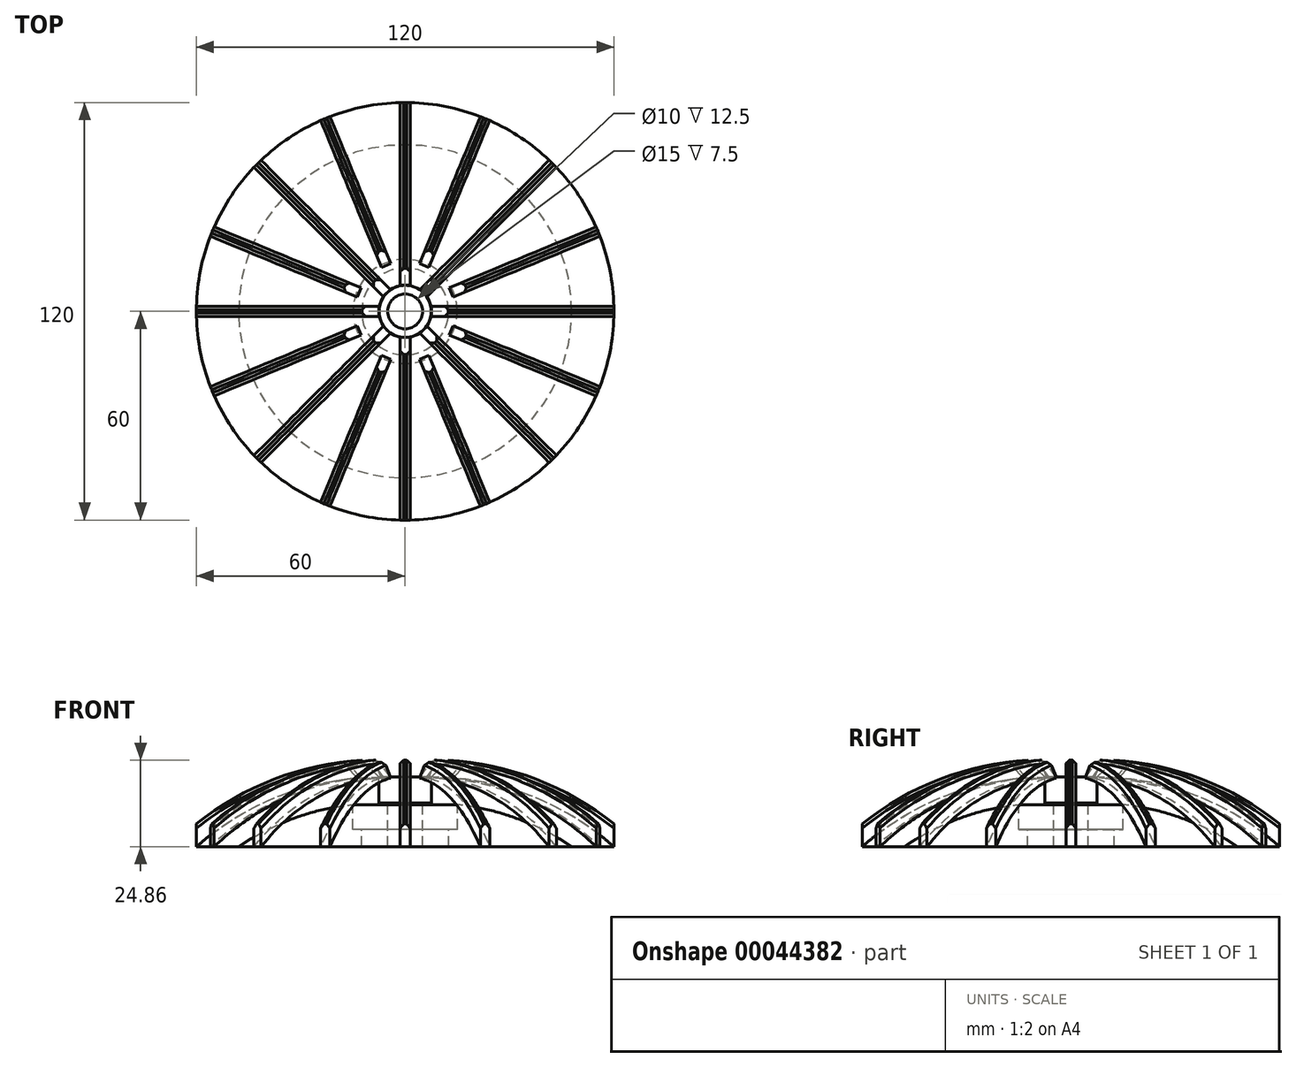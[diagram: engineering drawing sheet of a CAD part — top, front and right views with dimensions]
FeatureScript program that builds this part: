
annotation { "Feature Type Name" : "Feature", "Feature Type Description" : "" }
export const myFeature = defineFeature(function(context is Context, id is Id, definition is map)
    precondition{}
    {
        {
            var Q0;
            Q0=qCreatedBy(makeId("Right.planeOp"),FACE);
            var sketch = newSketch(context, id + "F0", { "sketchPlane" : qUnion([Q0])});
            skLineSegment(sketch, "E0", {"start": v(0, 38.83) * mm, "end": v(0, -39.1) * mm, "construction": true});
            skLineSegment(sketch, "E1", {"start": v(-69.96, 0) * mm, "end": v(68.9, 0) * mm, "construction": true});
            skLineSegment(sketch, "E2", {"start": v(-60, 0) * mm, "end": v(-47.86, 0) * mm});
            skLineSegment(sketch, "E3", {"start": v(-5, 0) * mm, "end": v(-5, 12.5) * mm});
            skLineSegment(sketch, "E4", {"start": v(-5, 12.5) * mm, "end": v(-7.5, 12.5) * mm});
            skLineSegment(sketch, "E5", {"start": v(-7.5, 12.5) * mm, "end": v(-7.5, 20) * mm});
            skLineSegment(sketch, "E6", {"start": v(-7.5, 20) * mm, "end": v(0, 20) * mm, "construction": true});
            skArc(sketch, "E7", {"start": v(-7.5, 20) * mm, "mid": v(-35.6, 14.83) * mm, "end": v(-60, 0) * mm});
            skArc(sketch, "E8.0", {"start": v(-15, 12.1) * mm, "mid": v(-32.18, 8.1) * mm, "end": v(-47.86, 0) * mm});
            skLineSegment(sketch, "E9.0", {"start": v(-2.5, 17.5) * mm, "end": v(-2.5, 20) * mm});
            skLineSegment(sketch, "E9.1", {"start": v(0, 17.5) * mm, "end": v(-2.5, 17.5) * mm});
            skLineSegment(sketch, "E9.2", {"start": v(0, 0) * mm, "end": v(0, 17.5) * mm});
            skLineSegment(sketch, "E10", {"start": v(-15, 12.1) * mm, "end": v(-15, 5) * mm});
            skLineSegment(sketch, "E11", {"start": v(-15, 5) * mm, "end": v(-12.5, 5) * mm});
            skLineSegment(sketch, "E12", {"start": v(-12.5, 5) * mm, "end": v(-12.5, 0) * mm});
            skLineSegment(sketch, "E13.trimOffspring", {"start": v(-12.5, 0) * mm, "end": v(-5, 0) * mm});
            skSolve(sketch);
        }
        {
            var Q0;
            Q0=makeQuery(id+"F0.imprint","IMPRINT",FACE,{"disambiguationData":[TD([[makeQuery(id+"F0.imprint","IMPRINT",EDGE,{"derivedFrom":sQuery(id+"F0.wireOp",EDGE,"E2")}),1.0]])]});
            var Q1;
            Q1=sQuery(id+"F0.wireOp",EDGE,"E0");
            revolve(context, id + "F1", {"entities" : qUnion([Q0]), "axis" : qUnion([Q1]), "revolveType" : RevolveType.FULL});
        }
        {
            var Q0;
            Q0=qCreatedBy(makeId("Right.planeOp"),FACE);
            var sketch = newSketch(context, id + "F2", { "sketchPlane" : qUnion([Q0])});
            skLineSegment(sketch, "E14.0", {"start": v(-7.5, 20) * mm, "end": v(7.5, 20) * mm, "construction": true});
            skLineSegment(sketch, "E15.0", {"start": v(-7.5, 12.5) * mm, "end": v(7.5, 12.5) * mm, "construction": true});
            skLineSegment(sketch, "E16.0", {"start": v(-60, 0) * mm, "end": v(60, 0) * mm, "construction": true});
            skArc(sketch, "E17", {"start": v(-7.5, 20) * mm, "mid": v(-35.6, 14.83) * mm, "end": v(-60, 0) * mm, "construction": true});
            skArc(sketch, "E18.0", {"start": v(-12.36, 24.86) * mm, "mid": v(-37.6, 19.41) * mm, "end": v(-60, 6.55) * mm});
            skArc(sketch, "E19.0", {"start": v(-7.5, 17) * mm, "mid": v(-32.9, 12.62) * mm, "end": v(-55.37, 0) * mm});
            skLineSegment(sketch, "E20", {"start": v(-60, 0) * mm, "end": v(-55.37, 0) * mm});
            skLineSegment(sketch, "E21", {"start": v(-60, 0) * mm, "end": v(-60, 6.55) * mm});
            skLineSegment(sketch, "E22", {"start": v(-7.5, 20) * mm, "end": v(-7.5, 17) * mm});
            skLineSegment(sketch, "E23", {"start": v(-7.5, 20) * mm, "end": v(-12.36, 24.86) * mm});
            skSolve(sketch);
        }
        {
            var Q0;
            Q0 = qSketchRegion(id + "F2", true);
            extrude(context, id + "F3", {"entities" : qUnion([Q0]), "endBound" : BoundingType.SYMMETRIC, "depth" : 2.9 * mm});
        }
        {
            var Q0;
            Q0=makeQuery(id+"F3.opExtrude","CAP_EDGE",EDGE,{"disambiguationData":[OSD([sQuery(id+"F2.wireOp",EDGE,"E18.0")])],"isStart":true});
            var Q1;
            Q1=makeQuery(id+"F3.opExtrude","CAP_EDGE",EDGE,{"disambiguationData":[OSD([sQuery(id+"F2.wireOp",EDGE,"E18.0")])],"isStart":false});
            chamfer(context, id + "F4", {"entities" : qUnion([Q0, Q1]), "width" : 1 * mm, "tangentPropagation" : true});
        }
        {
            var Q0;
            Q0=makeQuery(id+"F3.opExtrude","SWEPT_BODY",BODY,{"disambiguationData":[OSD([sQuery(id+"F2.wireOp",EDGE,"E18.0"),sQuery(id+"F2.wireOp",EDGE,"E19.0"),sQuery(id+"F2.wireOp",EDGE,"E20"),sQuery(id+"F2.wireOp",EDGE,"E21"),sQuery(id+"F2.wireOp",EDGE,"E22"),sQuery(id+"F2.wireOp",EDGE,"E23")])]});
            var Q1;
            Q1=makeQuery(id+"F1.opRevolve","SWEPT_FACE",FACE,{"disambiguationData":[OSD([sQuery(id+"F0.wireOp",EDGE,"E5")])]});
            circularPattern(context, id + "F5", {"entities" : qUnion([Q0]), "axis" : qUnion([Q1]), "angle" : 360 * degree, "instanceCount" : 8, "equalSpace" : true});
        }
        {
            var Q0;
            Q0=makeQuery(id+"F1.opRevolve","SWEPT_BODY",BODY,{"disambiguationData":[OSD([sQuery(id+"F0.wireOp",EDGE,"E2"),sQuery(id+"F0.wireOp",EDGE,"E3"),sQuery(id+"F0.wireOp",EDGE,"E4"),sQuery(id+"F0.wireOp",EDGE,"E5"),sQuery(id+"F0.wireOp",EDGE,"E7"),sQuery(id+"F0.wireOp",EDGE,"E8.0"),sQuery(id+"F0.wireOp",EDGE,"E10"),sQuery(id+"F0.wireOp",EDGE,"E11"),sQuery(id+"F0.wireOp",EDGE,"E12"),sQuery(id+"F0.wireOp",EDGE,"E13.trimOffspring")])]});
            var Q1;
            Q1=makeQuery(id+"F3.opExtrude","SWEPT_BODY",BODY,{"disambiguationData":[OSD([sQuery(id+"F2.wireOp",EDGE,"E18.0"),sQuery(id+"F2.wireOp",EDGE,"E19.0"),sQuery(id+"F2.wireOp",EDGE,"E20"),sQuery(id+"F2.wireOp",EDGE,"E21"),sQuery(id+"F2.wireOp",EDGE,"E22"),sQuery(id+"F2.wireOp",EDGE,"E23")])]});
            var Q2;
            Q2=makeQuery(id+"F5.opPattern","COPY",BODY,{"derivedFrom":makeQuery(id+"F3.opExtrude","SWEPT_BODY",BODY,{"disambiguationData":[OSD([sQuery(id+"F2.wireOp",EDGE,"E18.0"),sQuery(id+"F2.wireOp",EDGE,"E19.0"),sQuery(id+"F2.wireOp",EDGE,"E20"),sQuery(id+"F2.wireOp",EDGE,"E21"),sQuery(id+"F2.wireOp",EDGE,"E22"),sQuery(id+"F2.wireOp",EDGE,"E23")])]}),"instanceName":"1"});
            var Q3;
            Q3=makeQuery(id+"F5.opPattern","COPY",BODY,{"derivedFrom":makeQuery(id+"F3.opExtrude","SWEPT_BODY",BODY,{"disambiguationData":[OSD([sQuery(id+"F2.wireOp",EDGE,"E18.0"),sQuery(id+"F2.wireOp",EDGE,"E19.0"),sQuery(id+"F2.wireOp",EDGE,"E20"),sQuery(id+"F2.wireOp",EDGE,"E21"),sQuery(id+"F2.wireOp",EDGE,"E22"),sQuery(id+"F2.wireOp",EDGE,"E23")])]}),"instanceName":"2"});
            var Q4;
            Q4=makeQuery(id+"F5.opPattern","COPY",BODY,{"derivedFrom":makeQuery(id+"F3.opExtrude","SWEPT_BODY",BODY,{"disambiguationData":[OSD([sQuery(id+"F2.wireOp",EDGE,"E18.0"),sQuery(id+"F2.wireOp",EDGE,"E19.0"),sQuery(id+"F2.wireOp",EDGE,"E20"),sQuery(id+"F2.wireOp",EDGE,"E21"),sQuery(id+"F2.wireOp",EDGE,"E22"),sQuery(id+"F2.wireOp",EDGE,"E23")])]}),"instanceName":"3"});
            var Q5;
            Q5=makeQuery(id+"F5.opPattern","COPY",BODY,{"derivedFrom":makeQuery(id+"F3.opExtrude","SWEPT_BODY",BODY,{"disambiguationData":[OSD([sQuery(id+"F2.wireOp",EDGE,"E18.0"),sQuery(id+"F2.wireOp",EDGE,"E19.0"),sQuery(id+"F2.wireOp",EDGE,"E20"),sQuery(id+"F2.wireOp",EDGE,"E21"),sQuery(id+"F2.wireOp",EDGE,"E22"),sQuery(id+"F2.wireOp",EDGE,"E23")])]}),"instanceName":"4"});
            var Q6;
            Q6=makeQuery(id+"F5.opPattern","COPY",BODY,{"derivedFrom":makeQuery(id+"F3.opExtrude","SWEPT_BODY",BODY,{"disambiguationData":[OSD([sQuery(id+"F2.wireOp",EDGE,"E18.0"),sQuery(id+"F2.wireOp",EDGE,"E19.0"),sQuery(id+"F2.wireOp",EDGE,"E20"),sQuery(id+"F2.wireOp",EDGE,"E21"),sQuery(id+"F2.wireOp",EDGE,"E22"),sQuery(id+"F2.wireOp",EDGE,"E23")])]}),"instanceName":"5"});
            var Q7;
            Q7=makeQuery(id+"F5.opPattern","COPY",BODY,{"derivedFrom":makeQuery(id+"F3.opExtrude","SWEPT_BODY",BODY,{"disambiguationData":[OSD([sQuery(id+"F2.wireOp",EDGE,"E18.0"),sQuery(id+"F2.wireOp",EDGE,"E19.0"),sQuery(id+"F2.wireOp",EDGE,"E20"),sQuery(id+"F2.wireOp",EDGE,"E21"),sQuery(id+"F2.wireOp",EDGE,"E22"),sQuery(id+"F2.wireOp",EDGE,"E23")])]}),"instanceName":"6"});
            var Q8;
            Q8=makeQuery(id+"F5.opPattern","COPY",BODY,{"derivedFrom":makeQuery(id+"F3.opExtrude","SWEPT_BODY",BODY,{"disambiguationData":[OSD([sQuery(id+"F2.wireOp",EDGE,"E18.0"),sQuery(id+"F2.wireOp",EDGE,"E19.0"),sQuery(id+"F2.wireOp",EDGE,"E20"),sQuery(id+"F2.wireOp",EDGE,"E21"),sQuery(id+"F2.wireOp",EDGE,"E22"),sQuery(id+"F2.wireOp",EDGE,"E23")])]}),"instanceName":"7"});
            booleanBodies(context, id + "F6", {"operationType" : BooleanOperationType.UNION, "tools" : qUnion([Q0, Q1, Q2, Q3, Q4, Q5, Q6, Q7, Q8])});
        }
        {
            var Q0;
            Q0=makeQuery(id+"F1.opRevolve","SWEPT_FACE",FACE,{"disambiguationData":[OSD([sQuery(id+"F0.wireOp",EDGE,"E4")])]});
            var sketch = newSketch(context, id + "F7", { "sketchPlane" : qUnion([Q0])});
            skFitSpline(sketch, "E24.0.0", {"points": [v(-6.33, 4.28) * mm, v(-18.7, 16.65) * mm, v(-31.07, 29.02) * mm, v(-43.44, 41.39) * mm]});
            skArc(sketch, "E24.0.1", {"start": v(-43.44, 41.39) * mm, "mid": v(-55.43, 22.96) * mm, "end": v(-59.98, 1.45) * mm});
            skFitSpline(sketch, "E24.0.2", {"points": [v(-59.98, 1.45) * mm, v(-42.49, 1.45) * mm, v(-25, 1.45) * mm, v(-7.5, 1.45) * mm]});
            skFitSpline(sketch, "E24.0.3", {"points": [v(-7.5, 1.45) * mm, v(-7.5, 0.97) * mm, v(-7.5, 0.48) * mm, v(-7.5, 0) * mm]});
            skArc(sketch, "E24.0.4", {"start": v(-7.5, 0) * mm, "mid": v(-6.93, 2.87) * mm, "end": v(-5.3, 5.3) * mm});
            skFitSpline(sketch, "E24.0.5", {"points": [v(-5.3, 5.3) * mm, v(-5.65, 4.96) * mm, v(-5.99, 4.62) * mm, v(-6.33, 4.28) * mm]});
            skPoint(sketch, "E25.startSnap0", {"position": v(-6.93, 2.87) * mm});
            skLineSegment(sketch, "E26", {"start": v(-6.93, 2.87) * mm, "end": v(-55.43, 22.96) * mm});
            skLineSegment(sketch, "E27.0", {"start": v(-6.37, 4.2) * mm, "end": v(-54.88, 24.3) * mm});
            skLineSegment(sketch, "E28.0", {"start": v(-7.48, 1.53) * mm, "end": v(-55.99, 21.62) * mm});
            skLineSegment(sketch, "E29.0", {"start": v(-5.26, 6.89) * mm, "end": v(-53.77, 26.98) * mm});
            skLineSegment(sketch, "E30.0", {"start": v(-8.6, -1.15) * mm, "end": v(-57.1, 18.94) * mm});
            skLineSegment(sketch, "E31", {"start": v(-11.54, 9.49) * mm, "end": v(-14.87, 1.45) * mm});
            skSolve(sketch);
        }
        {
            var Q0;
            Q0=sQuery(id+"F7.wireOp",EDGE,"E26");
            cPlane(context, id + "F8", {"entities" : qUnion([Q0]), "cplaneType" : CPlaneType.LINE_ANGLE, "offset" : 150 * mm, "angle" : 0 * degree, "width" : 150 * mm, "height" : 150 * mm});
        }
        {
            var Q0;
            Q0=qCreatedBy(id+"F8.planeOp",FACE);
            var sketch = newSketch(context, id + "F9", { "sketchPlane" : qUnion([Q0])});
            skLineSegment(sketch, "E32", {"start": v(7.5, 20) * mm, "end": v(7.5, 12.5) * mm});
            skLineSegment(sketch, "E33", {"start": v(-7.5, 12.5) * mm, "end": v(-7.5, 20) * mm});
            skLineSegment(sketch, "E34.0.0", {"start": v(55.97, 0) * mm, "end": v(55.99, 0) * mm});
            skLineSegment(sketch, "E34.0.1", {"start": v(55.99, 0) * mm, "end": v(54.88, 0) * mm});
            skLineSegment(sketch, "E34.0.2", {"start": v(54.88, 0) * mm, "end": v(54.86, 0) * mm});
            skLineSegment(sketch, "E34.0.3", {"start": v(54.86, 0) * mm, "end": v(24.3, 0) * mm});
            skLineSegment(sketch, "E34.0.4", {"start": v(24.3, 0) * mm, "end": v(24.3, 0) * mm});
            skLineSegment(sketch, "E34.0.5", {"start": v(24.3, 0) * mm, "end": v(21.62, 0) * mm});
            skLineSegment(sketch, "E34.0.6", {"start": v(21.62, 0) * mm, "end": v(21.61, 0) * mm});
            skLineSegment(sketch, "E34.0.7", {"start": v(21.61, 0) * mm, "end": v(-21.61, 0) * mm});
            skLineSegment(sketch, "E34.0.8", {"start": v(-21.61, 0) * mm, "end": v(-21.62, 0) * mm});
            skLineSegment(sketch, "E34.0.9", {"start": v(-21.62, 0) * mm, "end": v(-24.3, 0) * mm});
            skLineSegment(sketch, "E34.0.10", {"start": v(-24.3, 0) * mm, "end": v(-24.3, 0) * mm});
            skLineSegment(sketch, "E34.0.11", {"start": v(-24.3, 0) * mm, "end": v(-54.86, 0) * mm});
            skLineSegment(sketch, "E34.0.12", {"start": v(-54.86, 0) * mm, "end": v(-54.88, 0) * mm});
            skLineSegment(sketch, "E34.0.13", {"start": v(-54.88, 0) * mm, "end": v(-55.99, 0) * mm});
            skLineSegment(sketch, "E34.0.14", {"start": v(-55.99, 0) * mm, "end": v(-55.97, 0) * mm});
            skLineSegment(sketch, "E34.0.15", {"start": v(-55.97, 0) * mm, "end": v(-60, 0) * mm});
            skLineSegment(sketch, "E34.0.16", {"start": v(-55.97, 0) * mm, "end": v(-55.99, 0) * mm});
            skLineSegment(sketch, "E34.0.17", {"start": v(-55.99, 0) * mm, "end": v(-54.88, 0) * mm});
            skLineSegment(sketch, "E34.0.18", {"start": v(-54.88, 0) * mm, "end": v(-54.86, 0) * mm});
            skLineSegment(sketch, "E34.0.19", {"start": v(-24.3, 0) * mm, "end": v(-54.86, 0) * mm});
            skLineSegment(sketch, "E34.0.20", {"start": v(-24.3, 0) * mm, "end": v(-24.3, 0) * mm});
            skLineSegment(sketch, "E34.0.21", {"start": v(-24.3, 0) * mm, "end": v(-21.62, 0) * mm});
            skLineSegment(sketch, "E34.0.22", {"start": v(-21.62, 0) * mm, "end": v(-21.61, 0) * mm});
            skLineSegment(sketch, "E34.0.23", {"start": v(21.61, 0) * mm, "end": v(-21.61, 0) * mm});
            skLineSegment(sketch, "E34.0.24", {"start": v(21.61, 0) * mm, "end": v(21.62, 0) * mm});
            skLineSegment(sketch, "E34.0.25", {"start": v(21.62, 0) * mm, "end": v(24.3, 0) * mm});
            skLineSegment(sketch, "E34.0.26", {"start": v(24.3, 0) * mm, "end": v(24.3, 0) * mm});
            skLineSegment(sketch, "E34.0.27", {"start": v(54.86, 0) * mm, "end": v(24.3, 0) * mm});
            skLineSegment(sketch, "E34.0.28", {"start": v(54.86, 0) * mm, "end": v(54.88, 0) * mm});
            skLineSegment(sketch, "E34.0.29", {"start": v(54.88, 0) * mm, "end": v(55.99, 0) * mm});
            skLineSegment(sketch, "E34.0.30", {"start": v(55.99, 0) * mm, "end": v(55.97, 0) * mm});
            skLineSegment(sketch, "E34.0.31", {"start": v(60, 0) * mm, "end": v(55.97, 0) * mm});
            skLineSegment(sketch, "E35", {"start": v(-7.5, 20) * mm, "end": v(7.5, 20) * mm});
            skPoint(sketch, "E36.0", {"position": v(-14.3, 12.5) * mm});
            skLineSegment(sketch, "E37", {"start": v(-14.3, 12.5) * mm, "end": v(-14.3, 32.48) * mm, "construction": true});
            skArc(sketch, "E38", {"start": v(-7.5, 20) * mm, "mid": v(-35.6, 14.83) * mm, "end": v(-60, 0) * mm, "construction": true});
            skArc(sketch, "E39", {"start": v(-14.3, 19.7) * mm, "mid": v(-38.74, 13.55) * mm, "end": v(-60, 0) * mm});
            skArc(sketch, "E40.0", {"start": v(-18.82, 24.23) * mm, "mid": v(-40.61, 18.2) * mm, "end": v(-60, 6.55) * mm});
            skArc(sketch, "E41.0", {"start": v(-14.3, 16.7) * mm, "mid": v(-36.08, 11.41) * mm, "end": v(-55.37, 0) * mm});
            skLineSegment(sketch, "E42", {"start": v(-14.3, 19.7) * mm, "end": v(-18.82, 24.23) * mm});
            skLineSegment(sketch, "E43", {"start": v(-60, 0) * mm, "end": v(-60, 6.55) * mm});
            skSolve(sketch);
        }
        {
            var Q0;
            Q0 = qSketchRegion(id + "F9", true);
            extrude(context, id + "F10", {"entities" : qUnion([Q0]), "endBound" : BoundingType.SYMMETRIC, "depth" : 2.9 * mm});
        }
        {
            var Q0;
            Q0=makeQuery(id+"F10.opExtrude","CAP_EDGE",EDGE,{"disambiguationData":[OSD([sQuery(id+"F9.wireOp",EDGE,"E40.0")])],"isStart":true});
            var Q1;
            Q1=makeQuery(id+"F10.opExtrude","CAP_EDGE",EDGE,{"disambiguationData":[OSD([sQuery(id+"F9.wireOp",EDGE,"E40.0")])],"isStart":false});
            chamfer(context, id + "F11", {"entities" : qUnion([Q0, Q1]), "width" : 1 * mm, "tangentPropagation" : true});
        }
        {
            var Q0;
            Q0=makeQuery(id+"F10.opExtrude","SWEPT_BODY",BODY,{"disambiguationData":[OSD([sQuery(id+"F9.wireOp",EDGE,"E39"),sQuery(id+"F9.wireOp",EDGE,"E40.0"),sQuery(id+"F9.wireOp",EDGE,"E42"),sQuery(id+"F9.wireOp",EDGE,"E43")])]});
            var Q1;
            Q1=makeQuery(id+"F1.opRevolve","SWEPT_FACE",FACE,{"disambiguationData":[OSD([sQuery(id+"F0.wireOp",EDGE,"E5")])]});
            circularPattern(context, id + "F12", {"entities" : qUnion([Q0]), "axis" : qUnion([Q1]), "angle" : 360 * degree, "instanceCount" : 8, "equalSpace" : true});
        }
    });
